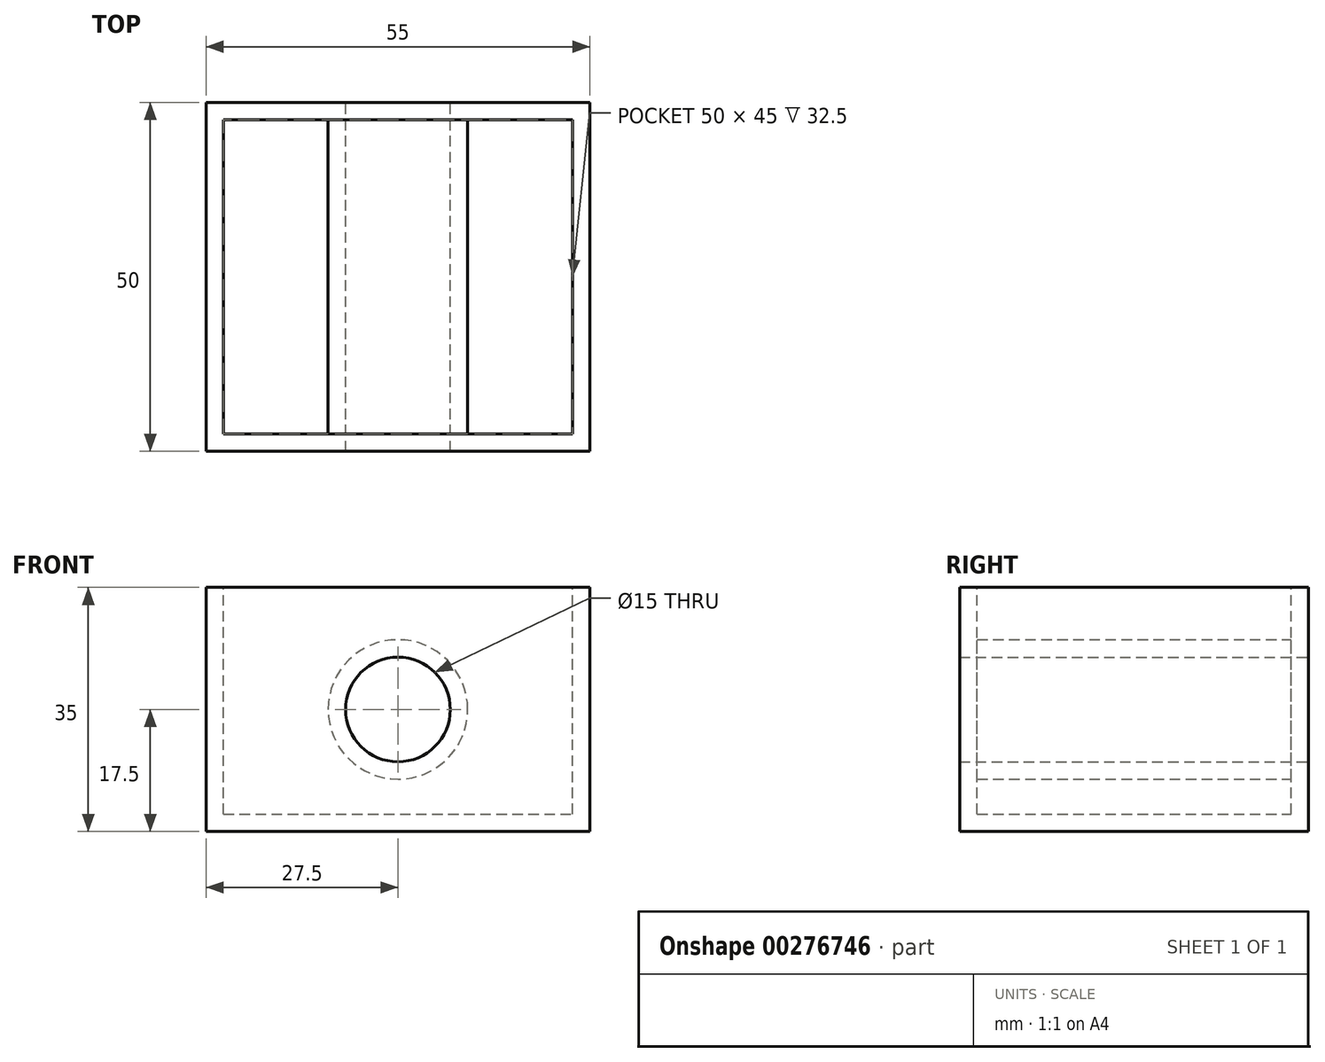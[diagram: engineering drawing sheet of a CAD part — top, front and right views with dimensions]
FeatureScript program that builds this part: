
annotation { "Feature Type Name" : "Feature", "Feature Type Description" : "" }
export const myFeature = defineFeature(function(context is Context, id is Id, definition is map)
    precondition{}
    {
        {
            var Q0;
            Q0=qCreatedBy(makeId("Front.planeOp"),FACE);
            var sketch = newSketch(context, id + "F0", { "sketchPlane" : qUnion([Q0])});
            skLineSegment(sketch, "E0.bottom", {"start": v(0, 0) * mm, "end": v(55, 0) * mm});
            skLineSegment(sketch, "E0.top", {"start": v(0, 35) * mm, "end": v(55, 35) * mm});
            skLineSegment(sketch, "E0.left", {"start": v(0, 0) * mm, "end": v(0, 35) * mm});
            skLineSegment(sketch, "E0.right", {"start": v(55, 0) * mm, "end": v(55, 35) * mm});
            skCircle(sketch, "E1", {"center": v(27.5, 17.5) * mm, "radius": 7.5 * mm});
            skPoint(sketch, "E1.centerSnap0", {"position": v(0, 17.5) * mm});
            skPoint(sketch, "E1.centerSnap1", {"position": v(27.5, 0) * mm});
            skSolve(sketch);
        }
        {
            var Q0;
            Q0 = qSketchRegion(id + "F0", true);
            extrude(context, id + "F1", {"entities" : qUnion([Q0]), "depth" : 50 * mm});
        }
        {
            var Q0;
            Q0=makeQuery(id+"F1.opExtrude","SWEPT_FACE",FACE,{"disambiguationData":[OSD([sQuery(id+"F0.wireOp",EDGE,"E0.top")])]});
            shell(context, id + "F2", {"entities" : qUnion([Q0]), "thickness" : 2.5 * mm});
        }
    });
